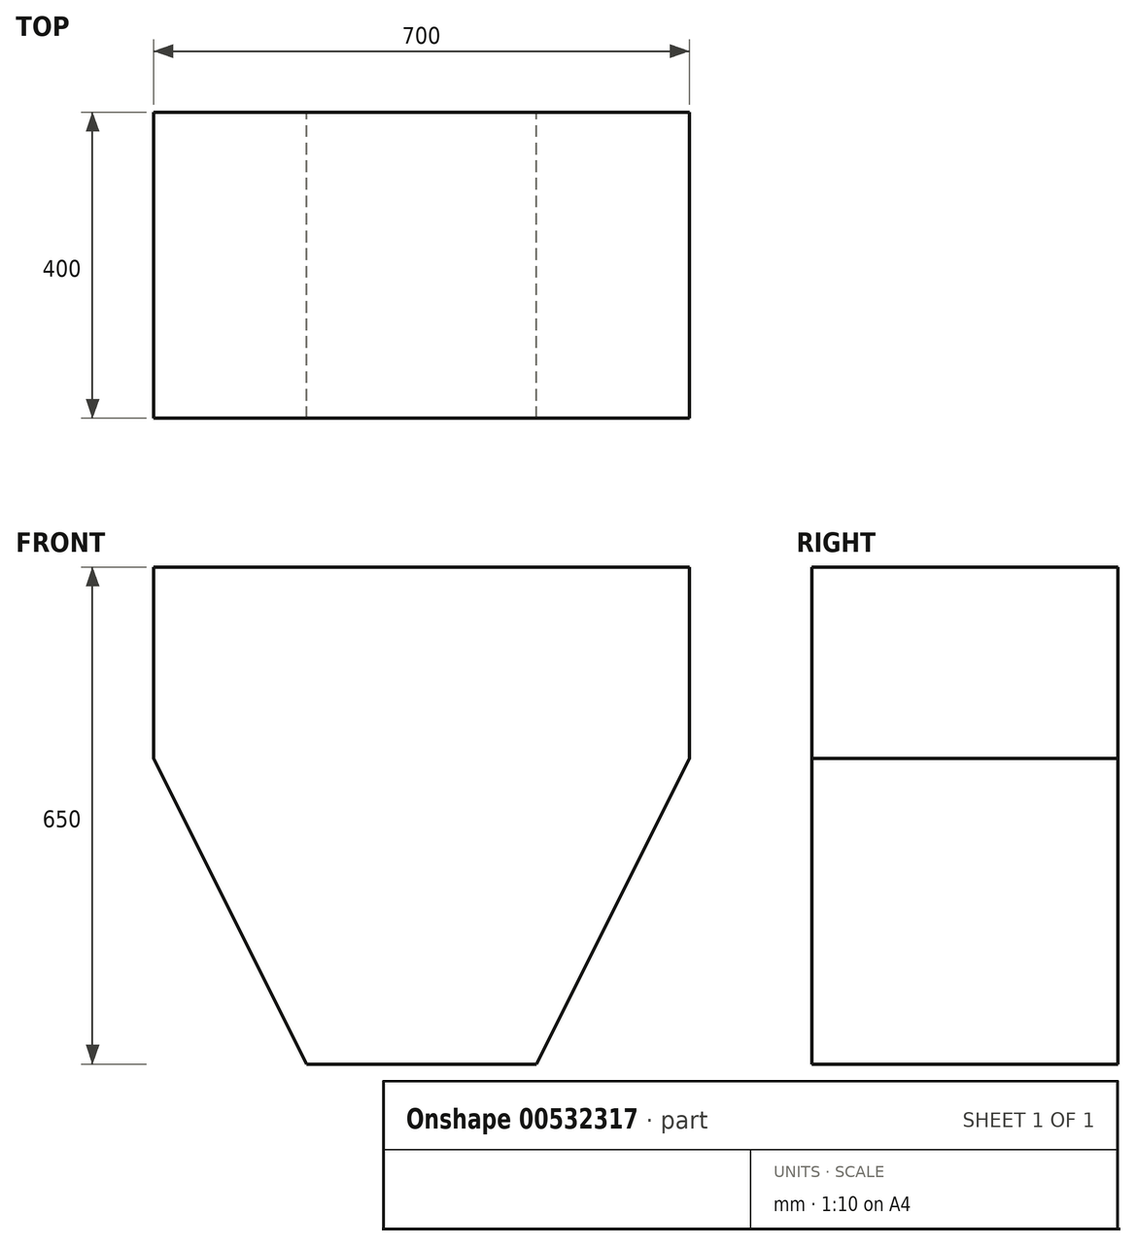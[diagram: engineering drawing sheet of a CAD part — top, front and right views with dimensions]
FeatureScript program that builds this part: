
annotation { "Feature Type Name" : "Feature", "Feature Type Description" : "" }
export const myFeature = defineFeature(function(context is Context, id is Id, definition is map)
    precondition{}
    {
        {
            var Q0;
            Q0=qCreatedBy(makeId("Front.planeOp"),FACE);
            var sketch = newSketch(context, id + "F0", { "sketchPlane" : qUnion([Q0])});
            skLineSegment(sketch, "E0.bottom", {"start": v(-350, 325) * mm, "end": v(350, 325) * mm});
            skLineSegment(sketch, "E0.top", {"start": v(-150, -325) * mm, "end": v(150, -325) * mm});
            skLineSegment(sketch, "E0.left", {"start": v(-350, 325) * mm, "end": v(-350, 75) * mm});
            skLineSegment(sketch, "E0.right", {"start": v(350, 325) * mm, "end": v(350, 75) * mm});
            skPoint(sketch, "E0.middle", {"position": v(0, 0) * mm});
            skLineSegment(sketch, "E1", {"start": v(-150, -325) * mm, "end": v(-350, 75) * mm});
            skLineSegment(sketch, "E2", {"start": v(150, -325) * mm, "end": v(350, 75) * mm});
            skPoint(sketch, "E3.orphan", {"position": v(-350, -325) * mm});
            skPoint(sketch, "E4.orphan", {"position": v(350, -325) * mm});
            skSolve(sketch);
        }
        {
            var Q0;
            Q0=makeQuery(id+"F0.imprint","IMPRINT",FACE,{"disambiguationData":[TD([[makeQuery(id+"F0.imprint","IMPRINT",EDGE,{"derivedFrom":sQuery(id+"F0.wireOp",EDGE,"E0.bottom")}),-1.0]])]});
            extrude(context, id + "F1", {"entities" : qUnion([Q0]), "depth" : 400 * mm, "offsetDistance" : 25 * mm});
        }
    });
